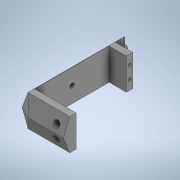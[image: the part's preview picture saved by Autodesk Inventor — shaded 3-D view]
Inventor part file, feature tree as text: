
AUTODESK INVENTOR PART (.ipt)
format: ipt  version: 2020 (Build 240168000, 168)  size: 361,984 bytes
history: native  units: in
note: dims shown in document units (in); Inventor stores cm internally (conversion verified against a paired STEP export)
features: sketch x16, extrude x11, plane x6, projected_geometry x6, loft x2, other x1
ambient origin geometry x8: Origin, YZ Plane, XZ Plane, XY Plane, X Axis, Y Axis, Z Axis, Center Point
bodies: Solid1 (feature_tree)
feature tree (42):
  sketch  "Sketch1"  dims[d1=1.1811in d2=3.5827in]
  plane  "Work Plane1"
  loft  "Loft1"
  extrude  "Extrusion1"  Depth=0.5906in
  extrude  "Extrusion2"  TaperAngle=0.0deg  [1 undecoded]
  extrude  "Extrusion3"  Depth=0.2362in
  extrude  "Extrusion4"  Depth=0.315in
  extrude  "Extrusion5"  TaperAngle=0.0deg  [1 undecoded]
  extrude  "Extrusion6"  TaperAngle=0.0deg  [1 undecoded]
  extrude  "Extrusion8"  Depth=0.315in
  sketch  "Sketch13"  dims[d24=0.0in d25=0.1181in]
  plane  "Work Plane2"
  plane  "Work Plane8"
  sketch  "Sketch14"  dims[d26=0.1181in d27=0.2362in]
  loft  "Loft2"
  sketch  "Sketch15"  dims[d28=0.2362in d29=0.1142in]
  extrude  "Extrusion9"  Depth=0.1181in
  plane  "Work Plane3"
  sketch  "Sketch18"  dims[d32=0.0in]
  plane  "Work Plane5"
  plane  "Work Plane7"
  extrude  "Extrusion10"  Depth=0.2362in
  extrude  "Extrusion11"  Depth=0.1142in
  extrude  "Extrusion12"  Depth=0.2756in
  sketch  "Sketch2"  dims[d3=1.1811in d5=0.5906in]
  sketch  "Sketch3"  dims[d6=0.5906in d7=0.0in d8=90.0deg]
  sketch  "Sketch4"  dims[d9=0.0in d10=90.0deg d11=0.2362in]
  sketch  "Sketch5"  dims[d12=0.2362in d13=0.315in]
  projected_geometry  "Projected Loop1"
  sketch  "Sketch6"  dims[d14=0.65in d15=0.0in]
  projected_geometry  "Projected Loop2"
  sketch  "Sketch8"  dims[d17=0.1654in d18=0.0in d19=0.0in]
  sketch  "Sketch9"  dims[d20=0.1575in d21=0.315in]
  projected_geometry  "Projected Loop6"
  sketch  "Sketch11"  dims[d22=0.0in d23=0.9055in]
  projected_geometry  "Projected Loop8"
  projected_geometry  "Projected Loop9"
  other  "Edges1"
  projected_geometry  "Projected Loop10"
  sketch  "Sketch17"  dims[d30=0.1142in d31=0.2756in]
  sketch  "Sketch19"  dims[d41=0.2756in d42=0.0in]
  sketch  "Sketch20"  dims[d48=0.1181in d49=0.1181in d50=0.0157in d51=0.5906in d52=0.0157in d53=0.2362in d56=0.122in d57=0.3543in d58=0.122in d59=0.3543in d60=1.2012in d61=1.2012in d62=0.2402in d63=0.2402in d64=0.0906in d65=-0.2061in d66=-0.0206in d67=0.0in d68=90.0deg d69=0.0in d70=90.0deg d71=1.9488in d72=0.2362in d73=0.3937in d74=0.0in d75=0.2362in d76=0.0884in d77=0.0in d78=0.3937in d79=0.0in d80=0.3937in d81=0.0in d82=0.0394in d4=0.0197in]
note: 3 required parameter values undecoded (feature->parameter linkage not recoverable at this tier; creation-order binding heuristic only, values carry confidence <= 0.55)
